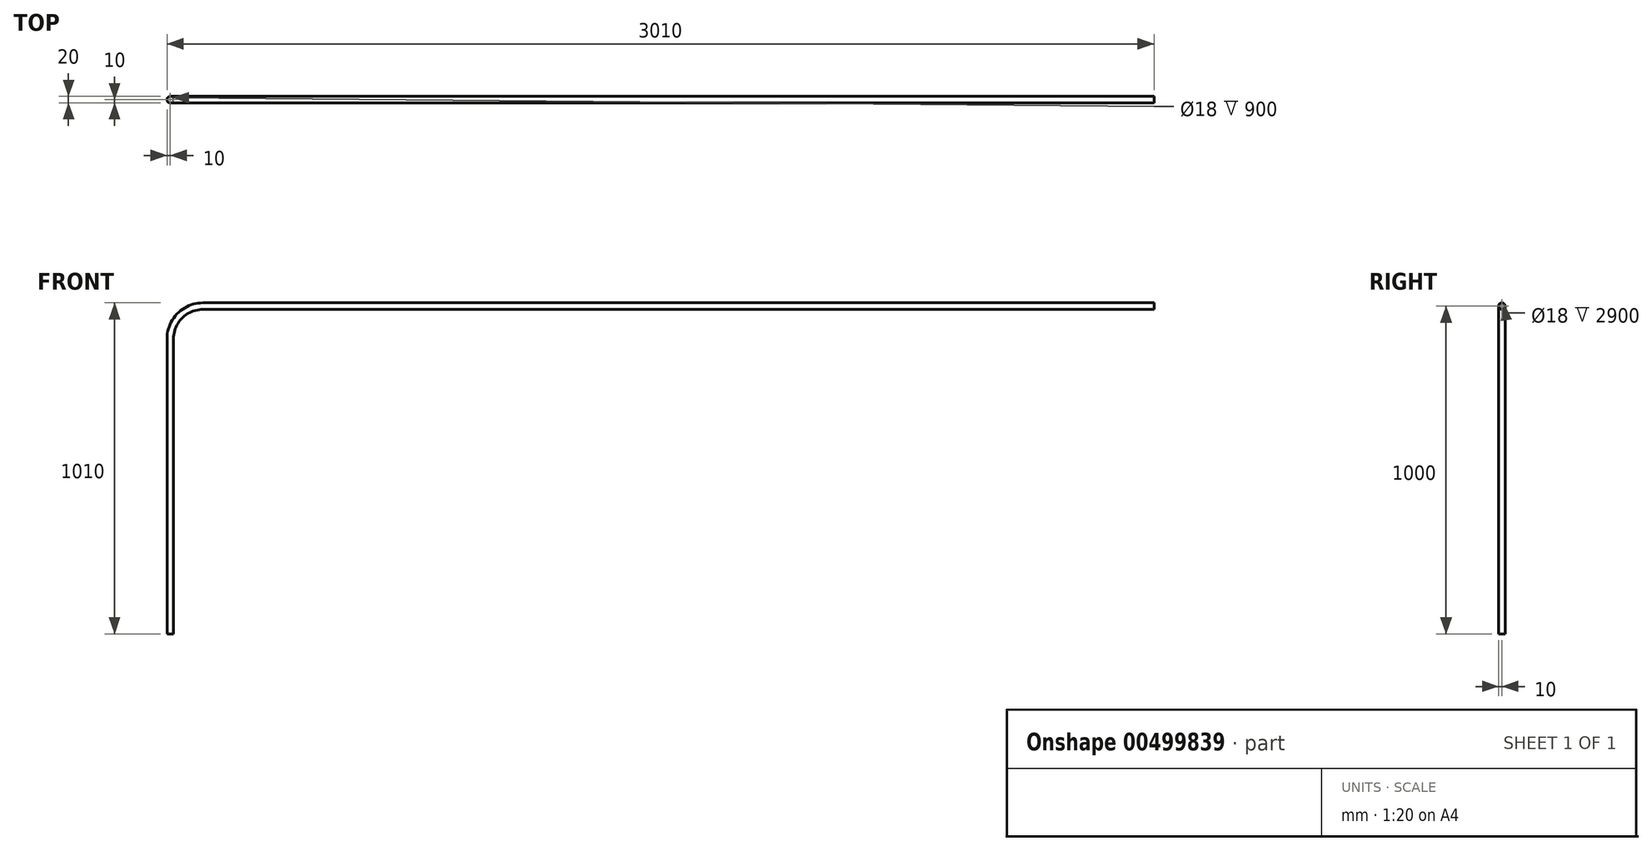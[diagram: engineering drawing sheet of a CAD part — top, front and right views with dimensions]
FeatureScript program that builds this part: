
annotation { "Feature Type Name" : "Feature", "Feature Type Description" : "" }
export const myFeature = defineFeature(function(context is Context, id is Id, definition is map)
    precondition{}
    {
        {
            var Q0;
            Q0=qCreatedBy(makeId("Front.planeOp"),FACE);
            var sketch = newSketch(context, id + "F0", { "sketchPlane" : qUnion([Q0])});
            skLineSegment(sketch, "E0", {"start": v(0, 0) * mm, "end": v(0, 900) * mm});
            skLineSegment(sketch, "E1", {"start": v(100, 1000) * mm, "end": v(3000, 1000) * mm});
            skPoint(sketch, "E2.visualSharp", {"position": v(0, 1000) * mm});
            skArc(sketch, "E2.filletArc", {"start": v(100, 1000) * mm, "mid": v(29.29, 970.71) * mm, "end": v(0, 900) * mm});
            skSolve(sketch);
        }
        {
            var Q0;
            Q0=qCreatedBy(makeId("Top.planeOp"),FACE);
            var sketch = newSketch(context, id + "F1", { "sketchPlane" : qUnion([Q0])});
            skCircle(sketch, "E3", {"center": v(0, 0) * mm, "radius": 10 * mm});
            skCircle(sketch, "E4", {"center": v(0, 0) * mm, "radius": 9 * mm});
            skSolve(sketch);
        }
        {
            var Q0;
            Q0=makeQuery(id+"F1.imprint","IMPRINT",FACE,{"disambiguationData":[TD([[makeQuery(id+"F1.imprint","IMPRINT",EDGE,{"derivedFrom":sQuery(id+"F1.wireOp",EDGE,"E3")}),1.0]])]});
            var Q1;
            Q1=sQuery(id+"F0.wireOp",EDGE,"E0");
            var Q2;
            Q2=sQuery(id+"F0.wireOp",EDGE,"E2.filletArc");
            var Q3;
            Q3=sQuery(id+"F0.wireOp",EDGE,"E1");
            sweep(context, id + "F2", {"profiles" : qUnion([Q0]), "path" : qUnion([Q1, Q2, Q3])});
        }
    });
